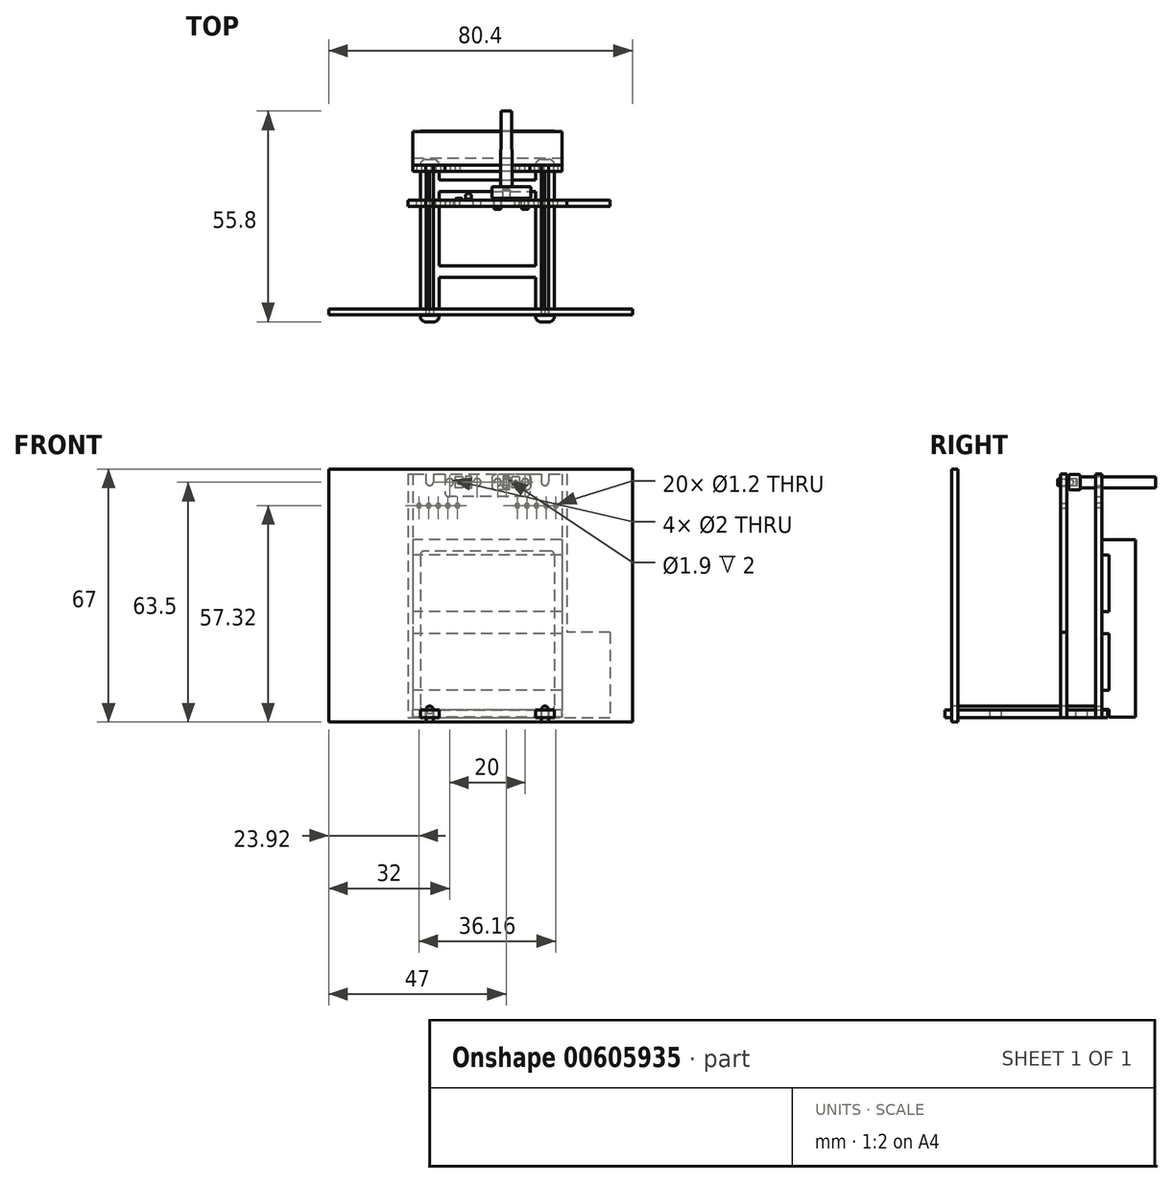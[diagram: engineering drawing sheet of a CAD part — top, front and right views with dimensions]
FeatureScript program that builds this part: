
annotation { "Feature Type Name" : "Feature", "Feature Type Description" : "" }
export const myFeature = defineFeature(function(context is Context, id is Id, definition is map)
    precondition{}
    {
        {
            var Q0;
            Q0=qCreatedBy(makeId("Top.planeOp"),FACE);
            var sketch = newSketch(context, id + "F0", { "sketchPlane" : qUnion([Q0])});
            skLineSegment(sketch, "E0", {"start": v(-17.75, -15.65) * mm, "end": v(-17.75, -13.85) * mm});
            skLineSegment(sketch, "E1", {"start": v(-17.75, -13.85) * mm, "end": v(-16.2, -13.85) * mm});
            skLineSegment(sketch, "E2", {"start": v(-16.2, -13.85) * mm, "end": v(-16.2, -12.2) * mm});
            skLineSegment(sketch, "E3", {"start": v(-16.2, -12.2) * mm, "end": v(-17.75, -12.2) * mm});
            skLineSegment(sketch, "E4", {"start": v(-14.3, -12.2) * mm, "end": v(-14.3, -13.85) * mm});
            skLineSegment(sketch, "E5", {"start": v(-14.3, -13.85) * mm, "end": v(-12.75, -13.85) * mm});
            skLineSegment(sketch, "E6", {"start": v(-12.75, -13.85) * mm, "end": v(-12.75, -15.65) * mm});
            skLineSegment(sketch, "E7", {"start": v(-12.75, -15.65) * mm, "end": v(-17.75, -15.65) * mm});
            skLineSegment(sketch, "E8", {"start": v(-12.75, -12.2) * mm, "end": v(-12.75, -3.84) * mm});
            skLineSegment(sketch, "E9", {"start": v(-12.75, -3.84) * mm, "end": v(12.75, -3.84) * mm});
            skLineSegment(sketch, "E10", {"start": v(17.75, 14.95) * mm, "end": v(16.2, 14.95) * mm});
            skLineSegment(sketch, "E11", {"start": v(16.2, 14.95) * mm, "end": v(16.2, 16.6) * mm});
            skLineSegment(sketch, "E12", {"start": v(16.2, 16.6) * mm, "end": v(17.75, 16.6) * mm});
            skLineSegment(sketch, "E13", {"start": v(17.75, 16.6) * mm, "end": v(17.75, 24.2) * mm});
            skLineSegment(sketch, "E14", {"start": v(12.75, 16.6) * mm, "end": v(14.3, 16.6) * mm});
            skLineSegment(sketch, "E15", {"start": v(14.3, 16.6) * mm, "end": v(14.3, 14.95) * mm});
            skLineSegment(sketch, "E16", {"start": v(14.3, 14.95) * mm, "end": v(12.75, 14.95) * mm});
            skLineSegment(sketch, "E17", {"start": v(-12.75, -0.84) * mm, "end": v(12.75, -0.84) * mm});
            skLineSegment(sketch, "E18", {"start": v(-17.75, 24.2) * mm, "end": v(-16.2, 24.2) * mm});
            skLineSegment(sketch, "E19", {"start": v(-16.2, 24.2) * mm, "end": v(-16.2, 25.85) * mm});
            skLineSegment(sketch, "E20", {"start": v(-16.2, 25.85) * mm, "end": v(-17.75, 25.85) * mm});
            skLineSegment(sketch, "E21", {"start": v(-17.75, 25.85) * mm, "end": v(-17.75, 27.35) * mm});
            skLineSegment(sketch, "E22", {"start": v(-17.75, 27.35) * mm, "end": v(-12.75, 27.35) * mm});
            skLineSegment(sketch, "E23", {"start": v(-12.75, 24.2) * mm, "end": v(-14.3, 24.2) * mm});
            skLineSegment(sketch, "E24", {"start": v(-14.3, 24.2) * mm, "end": v(-14.3, 25.85) * mm});
            skLineSegment(sketch, "E25", {"start": v(-14.3, 25.85) * mm, "end": v(-12.75, 25.85) * mm});
            skLineSegment(sketch, "E26", {"start": v(-12.75, 25.85) * mm, "end": v(-12.75, 27.35) * mm});
            skLineSegment(sketch, "E27", {"start": v(12.75, 24.2) * mm, "end": v(14.3, 24.2) * mm});
            skLineSegment(sketch, "E28", {"start": v(14.3, 25.85) * mm, "end": v(12.75, 25.85) * mm});
            skLineSegment(sketch, "E29", {"start": v(12.75, 25.85) * mm, "end": v(12.75, 27.35) * mm});
            skLineSegment(sketch, "E30", {"start": v(12.75, 27.35) * mm, "end": v(17.75, 27.35) * mm});
            skLineSegment(sketch, "E31", {"start": v(17.75, 24.2) * mm, "end": v(16.2, 24.2) * mm});
            skLineSegment(sketch, "E32", {"start": v(16.2, 24.2) * mm, "end": v(16.2, 25.85) * mm});
            skLineSegment(sketch, "E33", {"start": v(16.2, 25.85) * mm, "end": v(17.75, 25.85) * mm});
            skLineSegment(sketch, "E34", {"start": v(17.75, 25.85) * mm, "end": v(17.75, 27.35) * mm});
            skLineSegment(sketch, "E35", {"start": v(-12.75, -12.2) * mm, "end": v(-14.3, -12.2) * mm});
            skLineSegment(sketch, "E36", {"start": v(-12.75, 16.6) * mm, "end": v(-14.3, 16.6) * mm});
            skLineSegment(sketch, "E37", {"start": v(-14.3, 16.6) * mm, "end": v(-14.3, 14.95) * mm});
            skLineSegment(sketch, "E38", {"start": v(-14.3, 14.95) * mm, "end": v(-12.75, 14.95) * mm});
            skLineSegment(sketch, "E39", {"start": v(-12.75, -0.84) * mm, "end": v(-12.75, 14.95) * mm});
            skLineSegment(sketch, "E40", {"start": v(-17.75, 24.2) * mm, "end": v(-17.75, 16.6) * mm});
            skLineSegment(sketch, "E41", {"start": v(-17.75, 16.6) * mm, "end": v(-16.2, 16.6) * mm});
            skLineSegment(sketch, "E42", {"start": v(-16.2, 16.6) * mm, "end": v(-16.2, 14.95) * mm});
            skLineSegment(sketch, "E43", {"start": v(-16.2, 14.95) * mm, "end": v(-17.75, 14.95) * mm});
            skLineSegment(sketch, "E44", {"start": v(-17.75, 14.95) * mm, "end": v(-17.75, -12.2) * mm});
            skLineSegment(sketch, "E45", {"start": v(-12.75, 24.2) * mm, "end": v(-12.75, 21.9) * mm});
            skLineSegment(sketch, "E46", {"start": v(-12.75, 16.6) * mm, "end": v(-12.75, 18.82) * mm});
            skLineSegment(sketch, "E47", {"start": v(14.3, 25.85) * mm, "end": v(14.3, 24.2) * mm});
            skLineSegment(sketch, "E48", {"start": v(12.75, 24.2) * mm, "end": v(12.75, 21.9) * mm});
            skLineSegment(sketch, "E49", {"start": v(-12.75, 21.9) * mm, "end": v(12.75, 21.9) * mm});
            skLineSegment(sketch, "E50", {"start": v(-12.75, 18.82) * mm, "end": v(12.75, 18.82) * mm});
            skLineSegment(sketch, "E51", {"start": v(12.75, 16.6) * mm, "end": v(12.75, 18.82) * mm});
            skLineSegment(sketch, "E52", {"start": v(12.75, -0.84) * mm, "end": v(12.75, 14.95) * mm});
            skLineSegment(sketch, "E53", {"start": v(17.75, 14.95) * mm, "end": v(17.75, -12.2) * mm});
            skLineSegment(sketch, "E54", {"start": v(17.75, -12.2) * mm, "end": v(16.2, -12.2) * mm});
            skLineSegment(sketch, "E55", {"start": v(16.2, -12.2) * mm, "end": v(16.2, -13.85) * mm});
            skLineSegment(sketch, "E56", {"start": v(16.2, -13.85) * mm, "end": v(17.75, -13.85) * mm});
            skLineSegment(sketch, "E57", {"start": v(17.75, -13.85) * mm, "end": v(17.75, -15.65) * mm});
            skLineSegment(sketch, "E58", {"start": v(17.75, -15.65) * mm, "end": v(12.75, -15.65) * mm});
            skLineSegment(sketch, "E59", {"start": v(12.75, -15.65) * mm, "end": v(12.75, -13.85) * mm});
            skLineSegment(sketch, "E60", {"start": v(12.75, -13.85) * mm, "end": v(14.3, -13.85) * mm});
            skLineSegment(sketch, "E61", {"start": v(14.3, -13.85) * mm, "end": v(14.3, -12.2) * mm});
            skLineSegment(sketch, "E62", {"start": v(14.3, -12.2) * mm, "end": v(12.75, -12.2) * mm});
            skLineSegment(sketch, "E63", {"start": v(12.75, -12.2) * mm, "end": v(12.75, -3.84) * mm});
            skSolve(sketch);
        }
        {
            var Q0;
            Q0 = qSketchRegion(id + "F0", true);
            extrude(context, id + "F1", {"entities" : qUnion([Q0]), "depth" : 2 * mm, "offsetDistance" : 25 * mm});
        }
        {
            var Q0;
            Q0=makeQuery(id+"F1.opExtrude","SWEPT_EDGE",EDGE,{"disambiguationData":[OSD([sQuery(id+"F0.wireOp",EDGE,"E30"),sQuery(id+"F0.wireOp",EDGE,"E34")])]});
            var Q1;
            Q1=makeQuery(id+"F1.opExtrude","SWEPT_EDGE",EDGE,{"disambiguationData":[OSD([sQuery(id+"F0.wireOp",EDGE,"E29"),sQuery(id+"F0.wireOp",EDGE,"E30")])]});
            var Q2;
            Q2=makeQuery(id+"F1.opExtrude","SWEPT_EDGE",EDGE,{"disambiguationData":[OSD([sQuery(id+"F0.wireOp",EDGE,"E22"),sQuery(id+"F0.wireOp",EDGE,"E26")])]});
            var Q3;
            Q3=makeQuery(id+"F1.opExtrude","SWEPT_EDGE",EDGE,{"disambiguationData":[OSD([sQuery(id+"F0.wireOp",EDGE,"E21"),sQuery(id+"F0.wireOp",EDGE,"E22")])]});
            var Q4;
            Q4=makeQuery(id+"F1.opExtrude","SWEPT_EDGE",EDGE,{"disambiguationData":[OSD([sQuery(id+"F0.wireOp",EDGE,"6rP2uiYR-0tbi-BP4j-9BnD-fJcQIXdOzZpO"),sQuery(id+"F0.wireOp",EDGE,"r8ZNU0i4-ts59-kxLk-rAzM-9zbr7o6BRmU6")])]});
            var Q5;
            Q5=makeQuery(id+"F1.opExtrude","SWEPT_EDGE",EDGE,{"disambiguationData":[OSD([sQuery(id+"F0.wireOp",EDGE,"PC1FmKQ7-zntm-aZSk-GLTm-THbfAtVsDeOE"),sQuery(id+"F0.wireOp",EDGE,"6rP2uiYR-0tbi-BP4j-9BnD-fJcQIXdOzZpO")])]});
            var Q6;
            Q6=makeQuery(id+"F1.opExtrude","SWEPT_EDGE",EDGE,{"disambiguationData":[OSD([sQuery(id+"F0.wireOp",EDGE,"E6"),sQuery(id+"F0.wireOp",EDGE,"E7")])]});
            var Q7;
            Q7=makeQuery(id+"F1.opExtrude","SWEPT_EDGE",EDGE,{"disambiguationData":[OSD([sQuery(id+"F0.wireOp",EDGE,"E0"),sQuery(id+"F0.wireOp",EDGE,"E7")])]});
            var Q8;
            Q8=makeQuery(id+"F1.opExtrude","SWEPT_EDGE",EDGE,{"disambiguationData":[OSD([sQuery(id+"F0.wireOp",EDGE,"E57"),sQuery(id+"F0.wireOp",EDGE,"E58")])]});
            var Q9;
            Q9=makeQuery(id+"F1.opExtrude","SWEPT_EDGE",EDGE,{"disambiguationData":[OSD([sQuery(id+"F0.wireOp",EDGE,"E58"),sQuery(id+"F0.wireOp",EDGE,"E59")])]});
            fillet(context, id + "F2", {"entities" : qUnion([Q0, Q1, Q2, Q3, Q4, Q5, Q6, Q7, Q8, Q9]), "radius" : 1.5 * mm, "tangentPropagation" : true, "allowEdgeOverflow" : false});
        }
        {
            var Q0;
            Q0=makeQuery(id+"F1.opExtrude","CAP_FACE",FACE,{"disambiguationData":[OSD([sQuery(id+"F0.wireOp",EDGE,"E0"),sQuery(id+"F0.wireOp",EDGE,"E1"),sQuery(id+"F0.wireOp",EDGE,"E2"),sQuery(id+"F0.wireOp",EDGE,"E3"),sQuery(id+"F0.wireOp",EDGE,"E4"),sQuery(id+"F0.wireOp",EDGE,"E5"),sQuery(id+"F0.wireOp",EDGE,"E6"),sQuery(id+"F0.wireOp",EDGE,"E7"),sQuery(id+"F0.wireOp",EDGE,"E8"),sQuery(id+"F0.wireOp",EDGE,"E9"),sQuery(id+"F0.wireOp",EDGE,"E10"),sQuery(id+"F0.wireOp",EDGE,"E11"),sQuery(id+"F0.wireOp",EDGE,"E12"),sQuery(id+"F0.wireOp",EDGE,"E13"),sQuery(id+"F0.wireOp",EDGE,"E14"),sQuery(id+"F0.wireOp",EDGE,"E15"),sQuery(id+"F0.wireOp",EDGE,"E16"),sQuery(id+"F0.wireOp",EDGE,"E17"),sQuery(id+"F0.wireOp",EDGE,"E18"),sQuery(id+"F0.wireOp",EDGE,"E19"),sQuery(id+"F0.wireOp",EDGE,"E20"),sQuery(id+"F0.wireOp",EDGE,"E21"),sQuery(id+"F0.wireOp",EDGE,"E22"),sQuery(id+"F0.wireOp",EDGE,"E23"),sQuery(id+"F0.wireOp",EDGE,"E24"),sQuery(id+"F0.wireOp",EDGE,"E25"),sQuery(id+"F0.wireOp",EDGE,"E26"),sQuery(id+"F0.wireOp",EDGE,"E27"),sQuery(id+"F0.wireOp",EDGE,"E28"),sQuery(id+"F0.wireOp",EDGE,"E29"),sQuery(id+"F0.wireOp",EDGE,"E30"),sQuery(id+"F0.wireOp",EDGE,"E31"),sQuery(id+"F0.wireOp",EDGE,"E32"),sQuery(id+"F0.wireOp",EDGE,"E33"),sQuery(id+"F0.wireOp",EDGE,"E34"),sQuery(id+"F0.wireOp",EDGE,"E35"),sQuery(id+"F0.wireOp",EDGE,"E36"),sQuery(id+"F0.wireOp",EDGE,"E37"),sQuery(id+"F0.wireOp",EDGE,"E38"),sQuery(id+"F0.wireOp",EDGE,"E39"),sQuery(id+"F0.wireOp",EDGE,"E40"),sQuery(id+"F0.wireOp",EDGE,"E41"),sQuery(id+"F0.wireOp",EDGE,"E42"),sQuery(id+"F0.wireOp",EDGE,"E43"),sQuery(id+"F0.wireOp",EDGE,"E44"),sQuery(id+"F0.wireOp",EDGE,"E45"),sQuery(id+"F0.wireOp",EDGE,"E46"),sQuery(id+"F0.wireOp",EDGE,"E47"),sQuery(id+"F0.wireOp",EDGE,"E48"),sQuery(id+"F0.wireOp",EDGE,"E49"),sQuery(id+"F0.wireOp",EDGE,"E50"),sQuery(id+"F0.wireOp",EDGE,"E51"),sQuery(id+"F0.wireOp",EDGE,"E52"),sQuery(id+"F0.wireOp",EDGE,"E53"),sQuery(id+"F0.wireOp",EDGE,"E54"),sQuery(id+"F0.wireOp",EDGE,"E55"),sQuery(id+"F0.wireOp",EDGE,"E56"),sQuery(id+"F0.wireOp",EDGE,"E57"),sQuery(id+"F0.wireOp",EDGE,"E58"),sQuery(id+"F0.wireOp",EDGE,"E59"),sQuery(id+"F0.wireOp",EDGE,"E60"),sQuery(id+"F0.wireOp",EDGE,"E61"),sQuery(id+"F0.wireOp",EDGE,"E62"),sQuery(id+"F0.wireOp",EDGE,"E63")])],"isStart":false});
            var sketch = newSketch(context, id + "F3", { "sketchPlane" : qUnion([Q0])});
            skLineSegment(sketch, "E64.bottom", {"start": v(-16.2, 25.85) * mm, "end": v(-14.3, 25.85) * mm});
            skLineSegment(sketch, "E64.top", {"start": v(-16.2, -13.85) * mm, "end": v(-14.3, -13.85) * mm});
            skLineSegment(sketch, "E64.left", {"start": v(-16.2, 25.85) * mm, "end": v(-16.2, -13.85) * mm});
            skLineSegment(sketch, "E64.right", {"start": v(-14.3, 25.85) * mm, "end": v(-14.3, -13.85) * mm});
            skLineSegment(sketch, "E65.bottom", {"start": v(14.3, 25.85) * mm, "end": v(16.2, 25.85) * mm});
            skLineSegment(sketch, "E65.top", {"start": v(14.3, -13.85) * mm, "end": v(16.2, -13.85) * mm});
            skLineSegment(sketch, "E65.left", {"start": v(14.3, 25.85) * mm, "end": v(14.3, -13.85) * mm});
            skLineSegment(sketch, "E65.right", {"start": v(16.2, 25.85) * mm, "end": v(16.2, -13.85) * mm});
            skSolve(sketch);
        }
        {
            var Q0;
            Q0 = qSketchRegion(id + "F3", true);
            extrude(context, id + "F4", {"entities" : qUnion([Q0]), "operationType" : NewBodyOperationType.ADD, "depth" : 1 * mm, "offsetDistance" : 25 * mm});
        }
        {
            var Q0;
            Q0=makeQuery(id+"F4.opExtrude","CAP_EDGE",EDGE,{"disambiguationData":[OSD([sQuery(id+"F3.wireOp",EDGE,"E64.right")])],"isStart":false});
            var Q1;
            Q1=makeQuery(id+"F4.opExtrude","CAP_EDGE",EDGE,{"disambiguationData":[OSD([sQuery(id+"F3.wireOp",EDGE,"E64.left")])],"isStart":false});
            var Q2;
            Q2=makeQuery(id+"F4.opExtrude","CAP_EDGE",EDGE,{"disambiguationData":[OSD([sQuery(id+"F3.wireOp",EDGE,"E65.right")])],"isStart":false});
            var Q3;
            Q3=makeQuery(id+"F4.opExtrude","CAP_EDGE",EDGE,{"disambiguationData":[OSD([sQuery(id+"F3.wireOp",EDGE,"E65.left")])],"isStart":false});
            fillet(context, id + "F5", {"entities" : qUnion([Q0, Q1, Q2, Q3]), "radius" : 1 * mm, "tangentPropagation" : true, "allowEdgeOverflow" : false});
        }
        {
            var Q0;
            Q0=makeQuery(id+"F1.opExtrude","CAP_FACE",FACE,{"disambiguationData":[OSD([sQuery(id+"F0.wireOp",EDGE,"E0"),sQuery(id+"F0.wireOp",EDGE,"E1"),sQuery(id+"F0.wireOp",EDGE,"E2"),sQuery(id+"F0.wireOp",EDGE,"E3"),sQuery(id+"F0.wireOp",EDGE,"E4"),sQuery(id+"F0.wireOp",EDGE,"E5"),sQuery(id+"F0.wireOp",EDGE,"E6"),sQuery(id+"F0.wireOp",EDGE,"E7"),sQuery(id+"F0.wireOp",EDGE,"E8"),sQuery(id+"F0.wireOp",EDGE,"E9"),sQuery(id+"F0.wireOp",EDGE,"E10"),sQuery(id+"F0.wireOp",EDGE,"E11"),sQuery(id+"F0.wireOp",EDGE,"E12"),sQuery(id+"F0.wireOp",EDGE,"E13"),sQuery(id+"F0.wireOp",EDGE,"E14"),sQuery(id+"F0.wireOp",EDGE,"E15"),sQuery(id+"F0.wireOp",EDGE,"E16"),sQuery(id+"F0.wireOp",EDGE,"E17"),sQuery(id+"F0.wireOp",EDGE,"E18"),sQuery(id+"F0.wireOp",EDGE,"E19"),sQuery(id+"F0.wireOp",EDGE,"E20"),sQuery(id+"F0.wireOp",EDGE,"E21"),sQuery(id+"F0.wireOp",EDGE,"E22"),sQuery(id+"F0.wireOp",EDGE,"E23"),sQuery(id+"F0.wireOp",EDGE,"E24"),sQuery(id+"F0.wireOp",EDGE,"E25"),sQuery(id+"F0.wireOp",EDGE,"E26"),sQuery(id+"F0.wireOp",EDGE,"E27"),sQuery(id+"F0.wireOp",EDGE,"E28"),sQuery(id+"F0.wireOp",EDGE,"E29"),sQuery(id+"F0.wireOp",EDGE,"E30"),sQuery(id+"F0.wireOp",EDGE,"E31"),sQuery(id+"F0.wireOp",EDGE,"E32"),sQuery(id+"F0.wireOp",EDGE,"E33"),sQuery(id+"F0.wireOp",EDGE,"E34"),sQuery(id+"F0.wireOp",EDGE,"E35"),sQuery(id+"F0.wireOp",EDGE,"E36"),sQuery(id+"F0.wireOp",EDGE,"E37"),sQuery(id+"F0.wireOp",EDGE,"E38"),sQuery(id+"F0.wireOp",EDGE,"E39"),sQuery(id+"F0.wireOp",EDGE,"E40"),sQuery(id+"F0.wireOp",EDGE,"E41"),sQuery(id+"F0.wireOp",EDGE,"E42"),sQuery(id+"F0.wireOp",EDGE,"E43"),sQuery(id+"F0.wireOp",EDGE,"E44"),sQuery(id+"F0.wireOp",EDGE,"E45"),sQuery(id+"F0.wireOp",EDGE,"E46"),sQuery(id+"F0.wireOp",EDGE,"E47"),sQuery(id+"F0.wireOp",EDGE,"E48"),sQuery(id+"F0.wireOp",EDGE,"E49"),sQuery(id+"F0.wireOp",EDGE,"E50"),sQuery(id+"F0.wireOp",EDGE,"E51"),sQuery(id+"F0.wireOp",EDGE,"E52"),sQuery(id+"F0.wireOp",EDGE,"E53"),sQuery(id+"F0.wireOp",EDGE,"E54"),sQuery(id+"F0.wireOp",EDGE,"E55"),sQuery(id+"F0.wireOp",EDGE,"E56"),sQuery(id+"F0.wireOp",EDGE,"E57"),sQuery(id+"F0.wireOp",EDGE,"E58"),sQuery(id+"F0.wireOp",EDGE,"E59"),sQuery(id+"F0.wireOp",EDGE,"E60"),sQuery(id+"F0.wireOp",EDGE,"E61"),sQuery(id+"F0.wireOp",EDGE,"E62"),sQuery(id+"F0.wireOp",EDGE,"E63")])],"isStart":true});
            var sketch = newSketch(context, id + "F6", { "sketchPlane" : qUnion([Q0])});
            skLineSegment(sketch, "E66.bottom", {"start": v(-16.2, 13.85) * mm, "end": v(-14.3, 13.85) * mm});
            skLineSegment(sketch, "E66.top", {"start": v(-16.2, 12.2) * mm, "end": v(-14.3, 12.2) * mm});
            skLineSegment(sketch, "E66.left", {"start": v(-16.2, 13.85) * mm, "end": v(-16.2, 12.2) * mm});
            skLineSegment(sketch, "E66.right", {"start": v(-14.3, 13.85) * mm, "end": v(-14.3, 12.2) * mm});
            skLineSegment(sketch, "E67.bottom", {"start": v(14.3, 13.85) * mm, "end": v(16.2, 13.85) * mm});
            skLineSegment(sketch, "E67.top", {"start": v(14.3, 12.2) * mm, "end": v(16.2, 12.2) * mm});
            skLineSegment(sketch, "E67.left", {"start": v(14.3, 13.85) * mm, "end": v(14.3, 12.2) * mm});
            skLineSegment(sketch, "E67.right", {"start": v(16.2, 13.85) * mm, "end": v(16.2, 12.2) * mm});
            skSolve(sketch);
        }
        {
            var Q0;
            Q0 = qSketchRegion(id + "F6", true);
            extrude(context, id + "F7", {"entities" : qUnion([Q0]), "operationType" : NewBodyOperationType.ADD, "depth" : 1.25 * mm, "offsetDistance" : 25 * mm});
        }
        {
            var Q0;
            Q0=makeQuery(id+"F7.opExtrude","CAP_EDGE",EDGE,{"disambiguationData":[OSD([sQuery(id+"F6.wireOp",EDGE,"E66.right")])],"isStart":false});
            var Q1;
            Q1=makeQuery(id+"F7.opExtrude","CAP_EDGE",EDGE,{"disambiguationData":[OSD([sQuery(id+"F6.wireOp",EDGE,"E66.left")])],"isStart":false});
            var Q2;
            Q2=makeQuery(id+"F7.opExtrude","CAP_EDGE",EDGE,{"disambiguationData":[OSD([sQuery(id+"F6.wireOp",EDGE,"E67.right")])],"isStart":false});
            var Q3;
            Q3=makeQuery(id+"F7.opExtrude","CAP_EDGE",EDGE,{"disambiguationData":[OSD([sQuery(id+"F6.wireOp",EDGE,"E67.left")])],"isStart":false});
            fillet(context, id + "F8", {"entities" : qUnion([Q0, Q1, Q2, Q3]), "radius" : 0.3 * mm, "tangentPropagation" : true, "allowEdgeOverflow" : false});
        }
        {
            var Q0;
            {var subQ0=sQuery(id+"F0.wireOp",EDGE,"E54");var subQ1=sQuery(id+"F0.wireOp",EDGE,"E53");var subQ2=sQuery(id+"F0.wireOp",EDGE,"E52");var subQ3=sQuery(id+"F0.wireOp",EDGE,"E48");var subQ4=sQuery(id+"F0.wireOp",EDGE,"E47");var subQ5=sQuery(id+"F0.wireOp",EDGE,"E46");var subQ6=sQuery(id+"F0.wireOp",EDGE,"E45");var subQ7=sQuery(id+"F0.wireOp",EDGE,"E44");var subQ8=sQuery(id+"F0.wireOp",EDGE,"E43");var subQ9=sQuery(id+"F0.wireOp",EDGE,"E42");var subQ10=sQuery(id+"F0.wireOp",EDGE,"E41");var subQ11=sQuery(id+"F0.wireOp",EDGE,"E40");var subQ12=sQuery(id+"F0.wireOp",EDGE,"E39");var subQ13=sQuery(id+"F0.wireOp",EDGE,"E38");var subQ14=sQuery(id+"F0.wireOp",EDGE,"E37");var subQ15=sQuery(id+"F0.wireOp",EDGE,"E36");var subQ16=sQuery(id+"F0.wireOp",EDGE,"E35");var subQ17=sQuery(id+"F0.wireOp",EDGE,"E33");var subQ18=sQuery(id+"F0.wireOp",EDGE,"E32");var subQ19=sQuery(id+"F0.wireOp",EDGE,"E31");var subQ20=sQuery(id+"F0.wireOp",EDGE,"E30");var subQ21=sQuery(id+"F0.wireOp",EDGE,"E12");var subQ22=sQuery(id+"F0.wireOp",EDGE,"E11");var subQ23=sQuery(id+"F0.wireOp",EDGE,"E10");var subQ24=sQuery(id+"F0.wireOp",EDGE,"E9");var subQ25=sQuery(id+"F0.wireOp",EDGE,"E34");var subQ26=sQuery(id+"F0.wireOp",EDGE,"E13");var subQ27=sQuery(id+"F0.wireOp",EDGE,"E49");var subQ28=sQuery(id+"F0.wireOp",EDGE,"E2");var subQ29=sQuery(id+"F0.wireOp",EDGE,"E25");var subQ30=sQuery(id+"F0.wireOp",EDGE,"E14");var subQ31=sQuery(id+"F0.wireOp",EDGE,"E50");var subQ32=sQuery(id+"F0.wireOp",EDGE,"E3");var subQ33=sQuery(id+"F0.wireOp",EDGE,"E8");var subQ34=sQuery(id+"F0.wireOp",EDGE,"E29");var subQ35=sQuery(id+"F0.wireOp",EDGE,"E51");var subQ36=sQuery(id+"F0.wireOp",EDGE,"E4");var subQ37=sQuery(id+"F0.wireOp",EDGE,"E27");var subQ38=sQuery(id+"F0.wireOp",EDGE,"E15");var subQ39=sQuery(id+"F0.wireOp",EDGE,"E16");var subQ40=sQuery(id+"F0.wireOp",EDGE,"E17");var subQ41=sQuery(id+"F0.wireOp",EDGE,"E18");var subQ42=sQuery(id+"F0.wireOp",EDGE,"E19");var subQ43=sQuery(id+"F0.wireOp",EDGE,"E20");var subQ44=sQuery(id+"F0.wireOp",EDGE,"E22");var subQ45=sQuery(id+"F0.wireOp",EDGE,"E23");var subQ46=sQuery(id+"F0.wireOp",EDGE,"E24");var subQ47=sQuery(id+"F0.wireOp",EDGE,"E28");var subQ48=sQuery(id+"F0.wireOp",EDGE,"E55");var subQ49=sQuery(id+"F0.wireOp",EDGE,"E61");var subQ50=sQuery(id+"F0.wireOp",EDGE,"E62");var subQ51=sQuery(id+"F0.wireOp",EDGE,"E63");var subQ52=sQuery(id+"F0.wireOp",EDGE,"E21");var subQ53=sQuery(id+"F0.wireOp",EDGE,"E26");Q0=makeQuery(id+"F7.boolean.opBoolean","SPLIT",FACE,{"disambiguationData":[TD([makeQuery(id+"F1.opExtrude","SWEPT_FACE",FACE,{"disambiguationData":[OSD([subQ32])]})])],"derivedFrom":makeQuery(id+"F1.opExtrude","CAP_FACE",FACE,{"disambiguationData":[OSD([sQuery(id+"F0.wireOp",EDGE,"E0"),sQuery(id+"F0.wireOp",EDGE,"E1"),subQ28,subQ32,subQ36,sQuery(id+"F0.wireOp",EDGE,"E5"),sQuery(id+"F0.wireOp",EDGE,"E6"),sQuery(id+"F0.wireOp",EDGE,"E7"),subQ33,subQ24,subQ23,subQ22,subQ21,subQ26,subQ30,subQ38,subQ39,subQ40,subQ41,subQ42,subQ43,subQ52,subQ44,subQ45,subQ46,subQ29,subQ53,subQ37,subQ47,subQ34,subQ20,subQ19,subQ18,subQ17,subQ25,subQ16,subQ15,subQ14,subQ13,subQ12,subQ11,subQ10,subQ9,subQ8,subQ7,subQ6,subQ5,subQ4,subQ3,subQ27,subQ31,subQ35,subQ2,subQ1,subQ0,subQ48,sQuery(id+"F0.wireOp",EDGE,"E56"),sQuery(id+"F0.wireOp",EDGE,"E57"),sQuery(id+"F0.wireOp",EDGE,"E58"),sQuery(id+"F0.wireOp",EDGE,"E59"),sQuery(id+"F0.wireOp",EDGE,"E60"),subQ49,subQ50,subQ51])],"isStart":true})});}
            var sketch = newSketch(context, id + "F9", { "sketchPlane" : qUnion([Q0])});
            skLineSegment(sketch, "E68.bottom", {"start": v(-19.75, -24.22) * mm, "end": v(19.75, -24.22) * mm});
            skLineSegment(sketch, "E68.top", {"start": v(-19.75, -25.82) * mm, "end": v(19.75, -25.82) * mm});
            skLineSegment(sketch, "E68.left", {"start": v(-19.75, -24.22) * mm, "end": v(-19.75, -25.82) * mm});
            skLineSegment(sketch, "E68.right", {"start": v(19.75, -24.22) * mm, "end": v(19.75, -25.82) * mm});
            skSolve(sketch);
        }
        {
            var Q0;
            Q0 = qSketchRegion(id + "F9", true);
            extrude(context, id + "F10", {"entities" : qUnion([Q0]), "oppositeDirection" : true, "depth" : 64.5 * mm, "offsetDistance" : 25 * mm});
        }
        {
            var Q0;
            Q0=makeQuery(id+"F10.opExtrude","SWEPT_FACE",FACE,{"disambiguationData":[OSD([sQuery(id+"F9.wireOp",EDGE,"E68.top")])]});
            var sketch = newSketch(context, id + "F11", { "sketchPlane" : qUnion([Q0])});
            skLineSegment(sketch, "E69.bottom", {"start": v(-16.25, 0) * mm, "end": v(-14.25, 0) * mm});
            skLineSegment(sketch, "E69.left", {"start": v(-16.25, 0) * mm, "end": v(-16.25, 2) * mm});
            skLineSegment(sketch, "E69.right", {"start": v(-14.25, 0) * mm, "end": v(-14.25, 2) * mm});
            skArc(sketch, "E70", {"start": v(-14.25, 2) * mm, "mid": v(-15.25, 3.04) * mm, "end": v(-16.25, 2) * mm});
            skLineSegment(sketch, "E71.bottom", {"start": v(14.25, 0) * mm, "end": v(16.25, 0) * mm});
            skLineSegment(sketch, "E71.left", {"start": v(14.25, 0) * mm, "end": v(14.25, 2) * mm});
            skLineSegment(sketch, "E71.right", {"start": v(16.25, 0) * mm, "end": v(16.25, 2) * mm});
            skArc(sketch, "E72", {"start": v(16.25, 2) * mm, "mid": v(15.25, 3.04) * mm, "end": v(14.25, 2) * mm});
            skSolve(sketch);
        }
        {
            var Q0;
            Q0 = qSketchRegion(id + "F11", true);
            extrude(context, id + "F12", {"entities" : qUnion([Q0]), "operationType" : NewBodyOperationType.REMOVE, "oppositeDirection" : true, "depth" : 1.65 * mm, "offsetDistance" : 25 * mm});
        }
        {
            var Q0;
            Q0=makeQuery(id+"F10.opExtrude","SWEPT_FACE",FACE,{"disambiguationData":[OSD([sQuery(id+"F9.wireOp",EDGE,"E68.top")])]});
            var sketch = newSketch(context, id + "F13", { "sketchPlane" : qUnion([Q0])});
            skLineSegment(sketch, "E73.bottom", {"start": v(-11.25, 64.5) * mm, "end": v(11.25, 64.5) * mm});
            skLineSegment(sketch, "E73.top", {"start": v(-11.25, 58.5) * mm, "end": v(11.25, 58.5) * mm});
            skLineSegment(sketch, "E73.left", {"start": v(-11.25, 64.5) * mm, "end": v(-11.25, 58.5) * mm});
            skLineSegment(sketch, "E73.right", {"start": v(11.25, 64.5) * mm, "end": v(11.25, 58.5) * mm});
            skSolve(sketch);
        }
        {
            var Q0;
            Q0 = qSketchRegion(id + "F13", true);
            extrude(context, id + "F14", {"entities" : qUnion([Q0]), "operationType" : NewBodyOperationType.REMOVE, "oppositeDirection" : true, "depth" : 1.65 * mm, "offsetDistance" : 25 * mm});
        }
        {
            var Q0;
            Q0=makeQuery(id+"F10.opExtrude","SWEPT_FACE",FACE,{"disambiguationData":[OSD([sQuery(id+"F9.wireOp",EDGE,"E68.top")])]});
            var sketch = newSketch(context, id + "F15", { "sketchPlane" : qUnion([Q0])});
            skLineSegment(sketch, "E74.bottom", {"start": v(-16.25, 64.5) * mm, "end": v(-14.25, 64.5) * mm});
            skLineSegment(sketch, "E74.left", {"start": v(-16.25, 64.5) * mm, "end": v(-16.25, 62.4) * mm});
            skLineSegment(sketch, "E74.right", {"start": v(-14.25, 64.5) * mm, "end": v(-14.25, 62.4) * mm});
            skArc(sketch, "E75", {"start": v(-16.25, 62.4) * mm, "mid": v(-15.25, 61.4) * mm, "end": v(-14.25, 62.4) * mm});
            skLineSegment(sketch, "E76.bottom", {"start": v(14.25, 64.5) * mm, "end": v(16.25, 64.5) * mm});
            skLineSegment(sketch, "E76.left", {"start": v(14.25, 64.5) * mm, "end": v(14.25, 62.4) * mm});
            skLineSegment(sketch, "E76.right", {"start": v(16.25, 64.5) * mm, "end": v(16.25, 62.4) * mm});
            skArc(sketch, "E77", {"start": v(14.25, 62.4) * mm, "mid": v(15.25, 61.4) * mm, "end": v(16.25, 62.4) * mm});
            skSolve(sketch);
        }
        {
            var Q0;
            Q0 = qSketchRegion(id + "F15", true);
            extrude(context, id + "F16", {"entities" : qUnion([Q0]), "operationType" : NewBodyOperationType.REMOVE, "oppositeDirection" : true, "depth" : 1.65 * mm, "offsetDistance" : 25 * mm});
        }
        {
            var Q0;
            Q0=makeQuery(id+"F10.opExtrude","SWEPT_FACE",FACE,{"disambiguationData":[OSD([sQuery(id+"F9.wireOp",EDGE,"E68.top")])]});
            var sketch = newSketch(context, id + "F17", { "sketchPlane" : qUnion([Q0])});
            skLineSegment(sketch, "E78.bottom", {"start": v(-19.75, 47.1) * mm, "end": v(19.75, 47.1) * mm});
            skLineSegment(sketch, "E78.top", {"start": v(-19.75, 2.1) * mm, "end": v(19.75, 2.1) * mm});
            skLineSegment(sketch, "E78.left", {"start": v(-19.75, 47.1) * mm, "end": v(-19.75, 2.1) * mm});
            skLineSegment(sketch, "E78.right", {"start": v(19.75, 47.1) * mm, "end": v(19.75, 2.1) * mm});
            skSolve(sketch);
        }
        {
            var Q0;
            Q0 = qSketchRegion(id + "F17", true);
            extrude(context, id + "F18", {"entities" : qUnion([Q0]), "depth" : 8.9 * mm, "offsetDistance" : 25 * mm});
        }
        {
            var Q0;
            Q0=makeQuery(id+"F18.opExtrude","SWEPT_FACE",FACE,{"disambiguationData":[OSD([sQuery(id+"F17.wireOp",EDGE,"E78.top")])]});
            var sketch = newSketch(context, id + "F19", { "sketchPlane" : qUnion([Q0])});
            skLineSegment(sketch, "E79.bottom", {"start": v(-19.75, -34.72) * mm, "end": v(19.75, -34.72) * mm});
            skLineSegment(sketch, "E79.top", {"start": v(-19.75, -27.82) * mm, "end": v(19.75, -27.82) * mm});
            skLineSegment(sketch, "E79.left", {"start": v(-19.75, -34.72) * mm, "end": v(-19.75, -27.82) * mm});
            skLineSegment(sketch, "E79.right", {"start": v(19.75, -34.72) * mm, "end": v(19.75, -27.82) * mm});
            skSolve(sketch);
        }
        {
            var Q0;
            Q0 = qSketchRegion(id + "F19", true);
            extrude(context, id + "F20", {"entities" : qUnion([Q0]), "operationType" : NewBodyOperationType.ADD, "depth" : 2 * mm, "offsetDistance" : 25 * mm});
        }
        {
            var Q0;
            Q0=makeQuery(id+"F20.boolean.opBoolean","MERGE",FACE,{"derivedFrom":[makeQuery(id+"F18.opExtrude","SWEPT_FACE",FACE,{"disambiguationData":[OSD([sQuery(id+"F17.wireOp",EDGE,"E78.right")])]}),makeQuery(id+"F20.opExtrude","SWEPT_FACE",FACE,{"disambiguationData":[OSD([sQuery(id+"F19.wireOp",EDGE,"E79.left")])]})]});
            var sketch = newSketch(context, id + "F21", { "sketchPlane" : qUnion([Q0])});
            skLineSegment(sketch, "E80.bottom", {"start": v(-25.82, 22.2) * mm, "end": v(-27.82, 22.2) * mm});
            skLineSegment(sketch, "E80.top", {"start": v(-25.82, 7.2) * mm, "end": v(-27.82, 7.2) * mm});
            skLineSegment(sketch, "E80.left", {"start": v(-25.82, 22.2) * mm, "end": v(-25.82, 7.2) * mm});
            skLineSegment(sketch, "E80.right", {"start": v(-27.82, 22.2) * mm, "end": v(-27.82, 7.2) * mm});
            skLineSegment(sketch, "E81.bottom", {"start": v(-25.82, 43) * mm, "end": v(-27.82, 43) * mm});
            skLineSegment(sketch, "E81.top", {"start": v(-25.82, 28) * mm, "end": v(-27.82, 28) * mm});
            skLineSegment(sketch, "E81.left", {"start": v(-25.82, 43) * mm, "end": v(-25.82, 28) * mm});
            skLineSegment(sketch, "E81.right", {"start": v(-27.82, 43) * mm, "end": v(-27.82, 28) * mm});
            skSolve(sketch);
        }
        {
            var Q0;
            Q0 = qSketchRegion(id + "F21", true);
            extrude(context, id + "F22", {"entities" : qUnion([Q0]), "operationType" : NewBodyOperationType.REMOVE, "oppositeDirection" : true, "depth" : 39.5 * mm, "offsetDistance" : 25 * mm});
        }
        {
            var Q0;
            Q0=makeQuery(id+"F20.boolean.opBoolean","MERGE",FACE,{"derivedFrom":[makeQuery(id+"F18.opExtrude","CAP_FACE",FACE,{"disambiguationData":[OSD([sQuery(id+"F17.wireOp",EDGE,"E78.bottom"),sQuery(id+"F17.wireOp",EDGE,"E78.top"),sQuery(id+"F17.wireOp",EDGE,"E78.left"),sQuery(id+"F17.wireOp",EDGE,"E78.right")])],"isStart":false}),makeQuery(id+"F20.opExtrude","SWEPT_FACE",FACE,{"disambiguationData":[OSD([sQuery(id+"F19.wireOp",EDGE,"E79.bottom")])]})]});
            var sketch = newSketch(context, id + "F23", { "sketchPlane" : qUnion([Q0])});
            skLineSegment(sketch, "E82.bottom", {"start": v(-17.75, 44) * mm, "end": v(17.75, 44) * mm});
            skLineSegment(sketch, "E82.top", {"start": v(-17.75, 2) * mm, "end": v(17.75, 2) * mm});
            skLineSegment(sketch, "E82.left", {"start": v(-17.75, 44) * mm, "end": v(-17.75, 2) * mm});
            skLineSegment(sketch, "E82.right", {"start": v(17.75, 44) * mm, "end": v(17.75, 2) * mm});
            skSolve(sketch);
        }
        {
            var Q0;
            Q0 = qSketchRegion(id + "F23", true);
            extrude(context, id + "F24", {"entities" : qUnion([Q0]), "depth" : 0.1 * mm, "offsetDistance" : 25 * mm});
        }
        {
            var Q0;
            Q0=makeQuery(id+"F24.opExtrude","SWEPT_EDGE",EDGE,{"disambiguationData":[OSD([sQuery(id+"F23.wireOp",EDGE,"E82.top"),sQuery(id+"F23.wireOp",EDGE,"E82.left")])]});
            var Q1;
            Q1=makeQuery(id+"F24.opExtrude","SWEPT_EDGE",EDGE,{"disambiguationData":[OSD([sQuery(id+"F23.wireOp",EDGE,"E82.bottom"),sQuery(id+"F23.wireOp",EDGE,"E82.left")])]});
            var Q2;
            Q2=makeQuery(id+"F24.opExtrude","SWEPT_EDGE",EDGE,{"disambiguationData":[OSD([sQuery(id+"F23.wireOp",EDGE,"E82.bottom"),sQuery(id+"F23.wireOp",EDGE,"E82.right")])]});
            var Q3;
            Q3=makeQuery(id+"F24.opExtrude","SWEPT_EDGE",EDGE,{"disambiguationData":[OSD([sQuery(id+"F23.wireOp",EDGE,"E82.top"),sQuery(id+"F23.wireOp",EDGE,"E82.right")])]});
            fillet(context, id + "F25", {"entities" : qUnion([Q0, Q1, Q2, Q3]), "radius" : 1 * mm, "tangentPropagation" : true, "allowEdgeOverflow" : false});
        }
        {
            var Q0;
            {var subQ0=sQuery(id+"F0.wireOp",EDGE,"E54");var subQ1=sQuery(id+"F0.wireOp",EDGE,"E53");var subQ2=sQuery(id+"F0.wireOp",EDGE,"E52");var subQ3=sQuery(id+"F0.wireOp",EDGE,"E48");var subQ4=sQuery(id+"F0.wireOp",EDGE,"E47");var subQ5=sQuery(id+"F0.wireOp",EDGE,"E46");var subQ6=sQuery(id+"F0.wireOp",EDGE,"E45");var subQ7=sQuery(id+"F0.wireOp",EDGE,"E44");var subQ8=sQuery(id+"F0.wireOp",EDGE,"E43");var subQ9=sQuery(id+"F0.wireOp",EDGE,"E42");var subQ10=sQuery(id+"F0.wireOp",EDGE,"E41");var subQ11=sQuery(id+"F0.wireOp",EDGE,"E40");var subQ12=sQuery(id+"F0.wireOp",EDGE,"E39");var subQ13=sQuery(id+"F0.wireOp",EDGE,"E38");var subQ14=sQuery(id+"F0.wireOp",EDGE,"E37");var subQ15=sQuery(id+"F0.wireOp",EDGE,"E36");var subQ16=sQuery(id+"F0.wireOp",EDGE,"E35");var subQ17=sQuery(id+"F0.wireOp",EDGE,"E33");var subQ18=sQuery(id+"F0.wireOp",EDGE,"E32");var subQ19=sQuery(id+"F0.wireOp",EDGE,"E31");var subQ20=sQuery(id+"F0.wireOp",EDGE,"E30");var subQ21=sQuery(id+"F0.wireOp",EDGE,"E12");var subQ22=sQuery(id+"F0.wireOp",EDGE,"E11");var subQ23=sQuery(id+"F0.wireOp",EDGE,"E10");var subQ24=sQuery(id+"F0.wireOp",EDGE,"E9");var subQ25=sQuery(id+"F0.wireOp",EDGE,"E34");var subQ26=sQuery(id+"F0.wireOp",EDGE,"E13");var subQ27=sQuery(id+"F0.wireOp",EDGE,"E49");var subQ28=sQuery(id+"F0.wireOp",EDGE,"E2");var subQ29=sQuery(id+"F0.wireOp",EDGE,"E25");var subQ30=sQuery(id+"F0.wireOp",EDGE,"E14");var subQ31=sQuery(id+"F0.wireOp",EDGE,"E50");var subQ32=sQuery(id+"F0.wireOp",EDGE,"E3");var subQ33=sQuery(id+"F0.wireOp",EDGE,"E8");var subQ34=sQuery(id+"F0.wireOp",EDGE,"E29");var subQ35=sQuery(id+"F0.wireOp",EDGE,"E51");var subQ36=sQuery(id+"F0.wireOp",EDGE,"E4");var subQ37=sQuery(id+"F0.wireOp",EDGE,"E27");var subQ38=sQuery(id+"F0.wireOp",EDGE,"E15");var subQ39=sQuery(id+"F0.wireOp",EDGE,"E16");var subQ40=sQuery(id+"F0.wireOp",EDGE,"E17");var subQ41=sQuery(id+"F0.wireOp",EDGE,"E18");var subQ42=sQuery(id+"F0.wireOp",EDGE,"E19");var subQ43=sQuery(id+"F0.wireOp",EDGE,"E20");var subQ44=sQuery(id+"F0.wireOp",EDGE,"E22");var subQ45=sQuery(id+"F0.wireOp",EDGE,"E23");var subQ46=sQuery(id+"F0.wireOp",EDGE,"E24");var subQ47=sQuery(id+"F0.wireOp",EDGE,"E28");var subQ48=sQuery(id+"F0.wireOp",EDGE,"E55");var subQ49=sQuery(id+"F0.wireOp",EDGE,"E61");var subQ50=sQuery(id+"F0.wireOp",EDGE,"E62");var subQ51=sQuery(id+"F0.wireOp",EDGE,"E63");var subQ52=sQuery(id+"F0.wireOp",EDGE,"E21");var subQ53=sQuery(id+"F0.wireOp",EDGE,"E26");Q0=makeQuery(id+"F7.boolean.opBoolean","SPLIT",FACE,{"disambiguationData":[TD([makeQuery(id+"F1.opExtrude","SWEPT_FACE",FACE,{"disambiguationData":[OSD([subQ32])]})])],"derivedFrom":makeQuery(id+"F1.opExtrude","CAP_FACE",FACE,{"disambiguationData":[OSD([sQuery(id+"F0.wireOp",EDGE,"E0"),sQuery(id+"F0.wireOp",EDGE,"E1"),subQ28,subQ32,subQ36,sQuery(id+"F0.wireOp",EDGE,"E5"),sQuery(id+"F0.wireOp",EDGE,"E6"),sQuery(id+"F0.wireOp",EDGE,"E7"),subQ33,subQ24,subQ23,subQ22,subQ21,subQ26,subQ30,subQ38,subQ39,subQ40,subQ41,subQ42,subQ43,subQ52,subQ44,subQ45,subQ46,subQ29,subQ53,subQ37,subQ47,subQ34,subQ20,subQ19,subQ18,subQ17,subQ25,subQ16,subQ15,subQ14,subQ13,subQ12,subQ11,subQ10,subQ9,subQ8,subQ7,subQ6,subQ5,subQ4,subQ3,subQ27,subQ31,subQ35,subQ2,subQ1,subQ0,subQ48,sQuery(id+"F0.wireOp",EDGE,"E56"),sQuery(id+"F0.wireOp",EDGE,"E57"),sQuery(id+"F0.wireOp",EDGE,"E58"),sQuery(id+"F0.wireOp",EDGE,"E59"),sQuery(id+"F0.wireOp",EDGE,"E60"),subQ49,subQ50,subQ51])],"isStart":true})});}
            var sketch = newSketch(context, id + "F26", { "sketchPlane" : qUnion([Q0])});
            skLineSegment(sketch, "E83.bottom", {"start": v(-21, -14.97) * mm, "end": v(21, -14.97) * mm});
            skLineSegment(sketch, "E83.top", {"start": v(-21, -16.57) * mm, "end": v(21, -16.57) * mm});
            skLineSegment(sketch, "E83.left", {"start": v(-21, -14.97) * mm, "end": v(-21, -16.57) * mm});
            skLineSegment(sketch, "E83.right", {"start": v(21, -14.97) * mm, "end": v(21, -16.57) * mm});
            skSolve(sketch);
        }
        {
            var Q0;
            Q0 = qSketchRegion(id + "F26", true);
            extrude(context, id + "F27", {"entities" : qUnion([Q0]), "oppositeDirection" : true, "depth" : 64.5 * mm, "offsetDistance" : 25 * mm});
        }
        {
            var Q0;
            Q0=makeQuery(id+"F7.opExtrude","CAP_FACE",FACE,{"disambiguationData":[OSD([sQuery(id+"F6.wireOp",EDGE,"E66.bottom"),sQuery(id+"F6.wireOp",EDGE,"E66.top"),sQuery(id+"F6.wireOp",EDGE,"E66.left"),sQuery(id+"F6.wireOp",EDGE,"E66.right")])],"isStart":false});
            var sketch = newSketch(context, id + "F28", { "sketchPlane" : qUnion([Q0])});
            skLineSegment(sketch, "E84.bottom", {"start": v(-42, 13.82) * mm, "end": v(38.4, 13.82) * mm});
            skLineSegment(sketch, "E84.top", {"start": v(-42, 12.22) * mm, "end": v(38.4, 12.22) * mm});
            skLineSegment(sketch, "E84.left", {"start": v(-42, 13.82) * mm, "end": v(-42, 12.22) * mm});
            skLineSegment(sketch, "E84.right", {"start": v(38.4, 13.82) * mm, "end": v(38.4, 12.22) * mm});
            skSolve(sketch);
        }
        {
            var Q0;
            Q0 = qSketchRegion(id + "F28", true);
            extrude(context, id + "F29", {"entities" : qUnion([Q0]), "oppositeDirection" : true, "depth" : 67 * mm, "offsetDistance" : 25 * mm});
        }
        {
            var Q0;
            Q0=makeQuery(id+"F27.opExtrude","SWEPT_FACE",FACE,{"disambiguationData":[OSD([sQuery(id+"F26.wireOp",EDGE,"E83.top")])]});
            var sketch = newSketch(context, id + "F30", { "sketchPlane" : qUnion([Q0])});
            skLineSegment(sketch, "E85.bottom", {"start": v(-8.5, 63.75) * mm, "end": v(-6.5, 63.75) * mm});
            skLineSegment(sketch, "E85.top", {"start": v(-8.5, 60.75) * mm, "end": v(-6.5, 60.75) * mm});
            skLineSegment(sketch, "E85.left", {"start": v(-8.5, 63.75) * mm, "end": v(-8.5, 60.75) * mm});
            skLineSegment(sketch, "E85.right", {"start": v(-6.5, 63.75) * mm, "end": v(-6.5, 60.75) * mm});
            skLineSegment(sketch, "E86.bottom", {"start": v(6.5, 63.75) * mm, "end": v(8.5, 63.75) * mm});
            skLineSegment(sketch, "E86.top", {"start": v(6.5, 60.75) * mm, "end": v(8.5, 60.75) * mm});
            skLineSegment(sketch, "E86.left", {"start": v(6.5, 63.75) * mm, "end": v(6.5, 60.75) * mm});
            skLineSegment(sketch, "E86.right", {"start": v(8.5, 63.75) * mm, "end": v(8.5, 60.75) * mm});
            skSolve(sketch);
        }
        {
            var Q0;
            Q0 = qSketchRegion(id + "F30", true);
            extrude(context, id + "F31", {"entities" : qUnion([Q0]), "depth" : 0.38 * mm, "offsetDistance" : 25 * mm});
        }
        {
            var Q0;
            Q0=makeQuery(id+"F31.opExtrude","CAP_FACE",FACE,{"disambiguationData":[OSD([sQuery(id+"F30.wireOp",EDGE,"E85.bottom"),sQuery(id+"F30.wireOp",EDGE,"E85.top"),sQuery(id+"F30.wireOp",EDGE,"E85.left"),sQuery(id+"F30.wireOp",EDGE,"E85.right")])],"isStart":false});
            var sketch = newSketch(context, id + "F32", { "sketchPlane" : qUnion([Q0])});
            skCircle(sketch, "E87", {"center": v(-7.5, 62.25) * mm, "radius": 0.5 * mm});
            skCircle(sketch, "E88", {"center": v(7.5, 62.25) * mm, "radius": 0.5 * mm});
            skSolve(sketch);
        }
        {
            var Q0;
            Q0 = qSketchRegion(id + "F32", true);
            extrude(context, id + "F33", {"entities" : qUnion([Q0]), "depth" : 0.2 * mm, "offsetDistance" : 25 * mm});
        }
        {
            var Q0;
            Q0=makeQuery(id+"F33.opExtrude","CAP_EDGE",EDGE,{"disambiguationData":[OSD([sQuery(id+"F32.wireOp",EDGE,"E87")])],"isStart":false});
            var Q1;
            Q1=makeQuery(id+"F33.opExtrude","CAP_EDGE",EDGE,{"disambiguationData":[OSD([sQuery(id+"F32.wireOp",EDGE,"E88")])],"isStart":false});
            fillet(context, id + "F34", {"entities" : qUnion([Q0, Q1]), "radius" : 0.1 * mm, "tangentPropagation" : true, "allowEdgeOverflow" : false});
        }
        {
            var Q0;
            Q0=makeQuery(id+"F27.opExtrude","SWEPT_FACE",FACE,{"disambiguationData":[OSD([sQuery(id+"F26.wireOp",EDGE,"E83.top")])]});
            var sketch = newSketch(context, id + "F35", { "sketchPlane" : qUnion([Q0])});
            skLineSegment(sketch, "E89.bottom", {"start": v(-5.8, 63.85) * mm, "end": v(-4.2, 63.85) * mm});
            skLineSegment(sketch, "E89.top", {"start": v(-5.8, 60.65) * mm, "end": v(-4.2, 60.65) * mm});
            skLineSegment(sketch, "E89.left", {"start": v(-5.8, 63.85) * mm, "end": v(-5.8, 60.65) * mm});
            skLineSegment(sketch, "E89.right", {"start": v(-4.2, 63.85) * mm, "end": v(-4.2, 60.65) * mm});
            skLineSegment(sketch, "E90.bottom", {"start": v(4.2, 63.85) * mm, "end": v(5.8, 63.85) * mm});
            skLineSegment(sketch, "E90.top", {"start": v(4.2, 60.65) * mm, "end": v(5.8, 60.65) * mm});
            skLineSegment(sketch, "E90.left", {"start": v(4.2, 63.85) * mm, "end": v(4.2, 60.65) * mm});
            skLineSegment(sketch, "E90.right", {"start": v(5.8, 63.85) * mm, "end": v(5.8, 60.65) * mm});
            skSolve(sketch);
        }
        {
            var Q0;
            Q0 = qSketchRegion(id + "F35", true);
            extrude(context, id + "F36", {"entities" : qUnion([Q0]), "depth" : 0.25 * mm, "offsetDistance" : 25 * mm});
        }
        {
            var Q0;
            Q0=makeQuery(id+"F27.opExtrude","SWEPT_FACE",FACE,{"disambiguationData":[OSD([sQuery(id+"F26.wireOp",EDGE,"E83.top")])]});
            var sketch = newSketch(context, id + "F37", { "sketchPlane" : qUnion([Q0])});
            skLineSegment(sketch, "E91.bottom", {"start": v(-16.25, 64.5) * mm, "end": v(-14.25, 64.5) * mm});
            skLineSegment(sketch, "E91.left", {"start": v(-16.25, 64.5) * mm, "end": v(-16.25, 62.4) * mm});
            skLineSegment(sketch, "E91.right", {"start": v(-14.25, 64.5) * mm, "end": v(-14.25, 62.4) * mm});
            skLineSegment(sketch, "E92.bottom", {"start": v(14.25, 64.5) * mm, "end": v(16.25, 64.5) * mm});
            skLineSegment(sketch, "E92.left", {"start": v(14.25, 64.5) * mm, "end": v(14.25, 62.4) * mm});
            skLineSegment(sketch, "E92.right", {"start": v(16.25, 64.5) * mm, "end": v(16.25, 62.4) * mm});
            skArc(sketch, "E93", {"start": v(-16.25, 62.4) * mm, "mid": v(-15.25, 61.4) * mm, "end": v(-14.25, 62.4) * mm});
            skArc(sketch, "E94", {"start": v(14.25, 62.4) * mm, "mid": v(15.25, 61.4) * mm, "end": v(16.25, 62.4) * mm});
            skSolve(sketch);
        }
        {
            var Q0;
            Q0 = qSketchRegion(id + "F37", true);
            extrude(context, id + "F38", {"entities" : qUnion([Q0]), "operationType" : NewBodyOperationType.REMOVE, "oppositeDirection" : true, "depth" : 1.65 * mm, "offsetDistance" : 25 * mm});
        }
        {
            var Q0;
            Q0=makeQuery(id+"F27.opExtrude","SWEPT_FACE",FACE,{"disambiguationData":[OSD([sQuery(id+"F26.wireOp",EDGE,"E83.top")])]});
            var sketch = newSketch(context, id + "F39", { "sketchPlane" : qUnion([Q0])});
            skCircle(sketch, "E95", {"center": v(-2.7, 62.25) * mm, "radius": 1 * mm});
            skCircle(sketch, "E96", {"center": v(2.7, 62.25) * mm, "radius": 1 * mm});
            skCircle(sketch, "E97", {"center": v(-10, 62.25) * mm, "radius": 1 * mm});
            skCircle(sketch, "E98", {"center": v(10, 62.25) * mm, "radius": 1 * mm});
            skSolve(sketch);
        }
        {
            var Q0;
            Q0 = qSketchRegion(id + "F39", true);
            extrude(context, id + "F40", {"entities" : qUnion([Q0]), "operationType" : NewBodyOperationType.REMOVE, "oppositeDirection" : true, "depth" : 1.65 * mm, "offsetDistance" : 25 * mm});
        }
        {
            var Q0;
            Q0=makeQuery(id+"F36.opExtrude","CAP_FACE",FACE,{"disambiguationData":[OSD([sQuery(id+"F35.wireOp",EDGE,"E89.bottom"),sQuery(id+"F35.wireOp",EDGE,"E89.top"),sQuery(id+"F35.wireOp",EDGE,"E89.left"),sQuery(id+"F35.wireOp",EDGE,"E89.right")])],"isStart":false});
            var sketch = newSketch(context, id + "F41", { "sketchPlane" : qUnion([Q0])});
            skCircle(sketch, "E99", {"center": v(-5, 62.25) * mm, "radius": 0.8 * mm});
            skSolve(sketch);
        }
        {
            var Q0;
            Q0 = qSketchRegion(id + "F41", true);
            extrude(context, id + "F42", {"entities" : qUnion([Q0]), "operationType" : NewBodyOperationType.ADD, "depth" : 1.55 * mm, "offsetDistance" : 25 * mm});
        }
        {
            var Q0;
            Q0=makeQuery(id+"F42.opExtrude","CAP_EDGE",EDGE,{"disambiguationData":[OSD([sQuery(id+"F41.wireOp",EDGE,"E99")])],"isStart":false});
            fillet(context, id + "F43", {"entities" : qUnion([Q0]), "radius" : 0.8 * mm, "tangentPropagation" : true, "allowEdgeOverflow" : false});
        }
        {
            var Q0;
            Q0=makeQuery(id+"F36.opExtrude","CAP_FACE",FACE,{"disambiguationData":[OSD([sQuery(id+"F35.wireOp",EDGE,"E90.bottom"),sQuery(id+"F35.wireOp",EDGE,"E90.top"),sQuery(id+"F35.wireOp",EDGE,"E90.left"),sQuery(id+"F35.wireOp",EDGE,"E90.right")])],"isStart":false});
            var sketch = newSketch(context, id + "F44", { "sketchPlane" : qUnion([Q0])});
            skCircle(sketch, "E100", {"center": v(5, 62.25) * mm, "radius": 0.8 * mm});
            skSolve(sketch);
        }
        {
            var Q0;
            Q0 = qSketchRegion(id + "F44", true);
            extrude(context, id + "F45", {"entities" : qUnion([Q0]), "operationType" : NewBodyOperationType.ADD, "depth" : 1.55 * mm, "offsetDistance" : 25 * mm});
        }
        {
            var Q0;
            Q0=makeQuery(id+"F45.opExtrude","CAP_EDGE",EDGE,{"disambiguationData":[OSD([sQuery(id+"F44.wireOp",EDGE,"E100")])],"isStart":false});
            fillet(context, id + "F46", {"entities" : qUnion([Q0]), "radius" : 0.8 * mm, "tangentPropagation" : true, "allowEdgeOverflow" : false});
        }
        {
            var Q0;
            Q0=makeQuery(id+"F14.boolean.opBoolean","COPY",EDGE,{"derivedFrom":makeQuery(id+"F14.opExtrude","SWEPT_EDGE",EDGE,{"disambiguationData":[OSD([sQuery(id+"F13.wireOp",EDGE,"E73.top"),sQuery(id+"F13.wireOp",EDGE,"E73.left")])]})});
            var Q1;
            Q1=makeQuery(id+"F14.boolean.opBoolean","COPY",EDGE,{"derivedFrom":makeQuery(id+"F14.opExtrude","SWEPT_EDGE",EDGE,{"disambiguationData":[OSD([sQuery(id+"F13.wireOp",EDGE,"E73.top"),sQuery(id+"F13.wireOp",EDGE,"E73.right")])]})});
            fillet(context, id + "F47", {"entities" : qUnion([Q0, Q1]), "radius" : 1 * mm, "tangentPropagation" : true, "allowEdgeOverflow" : false});
        }
        {
            var Q0;
            Q0 = qSketchRegion(id + "F39", true);
            extrude(context, id + "F48", {"entities" : qUnion([Q0]), "operationType" : NewBodyOperationType.REMOVE, "oppositeDirection" : true, "depth" : 1.65 * mm, "offsetDistance" : 25 * mm});
        }
        {
            var Q0;
            Q0=makeQuery(id+"F33.opExtrude","CAP_FACE",FACE,{"disambiguationData":[OSD([sQuery(id+"F32.wireOp",EDGE,"E87")])],"isStart":false});
            var sketch = newSketch(context, id + "F49", { "sketchPlane" : qUnion([Q0])});
            skLineSegment(sketch, "E101.bottom", {"start": v(-11.5, 64.28) * mm, "end": v(-1.2, 64.28) * mm});
            skLineSegment(sketch, "E101.top", {"start": v(-11.5, 60.28) * mm, "end": v(-1.2, 60.28) * mm});
            skLineSegment(sketch, "E101.left", {"start": v(-11.5, 64.28) * mm, "end": v(-11.5, 60.28) * mm});
            skLineSegment(sketch, "E101.right", {"start": v(-1.2, 64.28) * mm, "end": v(-1.2, 60.28) * mm});
            skSolve(sketch);
        }
        {
            var Q0;
            Q0 = qSketchRegion(id + "F49", true);
            extrude(context, id + "F50", {"entities" : qUnion([Q0]), "depth" : 3 * mm, "offsetDistance" : 25 * mm});
        }
        {
            var Q0;
            Q0=makeQuery(id+"F50.opExtrude","CAP_FACE",FACE,{"disambiguationData":[OSD([sQuery(id+"F49.wireOp",EDGE,"E101.bottom"),sQuery(id+"F49.wireOp",EDGE,"E101.top"),sQuery(id+"F49.wireOp",EDGE,"E101.left"),sQuery(id+"F49.wireOp",EDGE,"E101.right")])],"isStart":false});
            var sketch = newSketch(context, id + "F51", { "sketchPlane" : qUnion([Q0])});
            skCircle(sketch, "E102", {"center": v(-5, 62.25) * mm, "radius": 1.5 * mm});
            skSolve(sketch);
        }
        {
            var Q0;
            Q0 = qSketchRegion(id + "F51", true);
            extrude(context, id + "F52", {"entities" : qUnion([Q0]), "operationType" : NewBodyOperationType.ADD, "depth" : 20 * mm, "offsetDistance" : 25 * mm, "hasDraft" : true, "draftAngle" : 0.2 * degree, "draftPullDirection" : true});
        }
        {
            var Q0;
            Q0=makeQuery(id+"F50.opExtrude","CAP_FACE",FACE,{"disambiguationData":[OSD([sQuery(id+"F49.wireOp",EDGE,"E101.bottom"),sQuery(id+"F49.wireOp",EDGE,"E101.top"),sQuery(id+"F49.wireOp",EDGE,"E101.left"),sQuery(id+"F49.wireOp",EDGE,"E101.right")])],"isStart":true});
            var sketch = newSketch(context, id + "F53", { "sketchPlane" : qUnion([Q0])});
            skCircle(sketch, "E103", {"center": v(2.7, 62.25) * mm, "radius": 0.9 * mm});
            skCircle(sketch, "E104", {"center": v(10, 62.25) * mm, "radius": 0.9 * mm});
            skSolve(sketch);
        }
        {
            var Q0;
            Q0 = qSketchRegion(id + "F53", true);
            extrude(context, id + "F54", {"entities" : qUnion([Q0]), "operationType" : NewBodyOperationType.ADD, "depth" : 3 * mm, "offsetDistance" : 25 * mm, "hasDraft" : true, "draftAngle" : 0.3 * degree, "draftPullDirection" : true});
        }
        {
            var Q0;
            Q0=makeQuery(id+"F54.opExtrude","CAP_EDGE",EDGE,{"disambiguationData":[OSD([sQuery(id+"F53.wireOp",EDGE,"E103")])],"isStart":false});
            var Q1;
            Q1=makeQuery(id+"F54.opExtrude","CAP_EDGE",EDGE,{"disambiguationData":[OSD([sQuery(id+"F53.wireOp",EDGE,"E104")])],"isStart":false});
            fillet(context, id + "F55", {"entities" : qUnion([Q0, Q1]), "radius" : 0.3 * mm, "tangentPropagation" : true, "allowEdgeOverflow" : false});
        }
        {
            var Q0;
            Q0=makeQuery(id+"F50.opExtrude","CAP_FACE",FACE,{"disambiguationData":[OSD([sQuery(id+"F49.wireOp",EDGE,"E101.bottom"),sQuery(id+"F49.wireOp",EDGE,"E101.top"),sQuery(id+"F49.wireOp",EDGE,"E101.left"),sQuery(id+"F49.wireOp",EDGE,"E101.right")])],"isStart":true});
            var sketch = newSketch(context, id + "F56", { "sketchPlane" : qUnion([Q0])});
            skCircle(sketch, "E105", {"center": v(5, 62.25) * mm, "radius": 0.95 * mm});
            skSolve(sketch);
        }
        {
            var Q0;
            Q0 = qSketchRegion(id + "F56", true);
            extrude(context, id + "F57", {"entities" : qUnion([Q0]), "operationType" : NewBodyOperationType.REMOVE, "oppositeDirection" : true, "depth" : 2 * mm, "offsetDistance" : 25 * mm});
        }
        {
            var Q0;
            Q0=makeQuery(id+"F50.opExtrude","CAP_FACE",FACE,{"disambiguationData":[OSD([sQuery(id+"F49.wireOp",EDGE,"E101.bottom"),sQuery(id+"F49.wireOp",EDGE,"E101.top"),sQuery(id+"F49.wireOp",EDGE,"E101.left"),sQuery(id+"F49.wireOp",EDGE,"E101.right")])],"isStart":true});
            var sketch = newSketch(context, id + "F58", { "sketchPlane" : qUnion([Q0])});
            skCircle(sketch, "E106", {"center": v(5, 62.25) * mm, "radius": 0.95 * mm});
            skSolve(sketch);
        }
        {
            var Q0;
            Q0 = qSketchRegion(id + "F58", true);
            extrude(context, id + "F59", {"entities" : qUnion([Q0]), "operationType" : NewBodyOperationType.REMOVE, "oppositeDirection" : true, "depth" : 2.2 * mm, "offsetDistance" : 25 * mm, "hasDraft" : true, "draftAngle" : 0.3 * degree, "draftPullDirection" : true});
        }
        {
            var Q0;
            Q0=makeQuery(id+"F50.opExtrude","SWEPT_EDGE",EDGE,{"disambiguationData":[OSD([sQuery(id+"F49.wireOp",EDGE,"E101.bottom"),sQuery(id+"F49.wireOp",EDGE,"E101.right")])]});
            var Q1;
            Q1=makeQuery(id+"F50.opExtrude","SWEPT_EDGE",EDGE,{"disambiguationData":[OSD([sQuery(id+"F49.wireOp",EDGE,"E101.bottom"),sQuery(id+"F49.wireOp",EDGE,"E101.left")])]});
            var Q2;
            Q2=makeQuery(id+"F50.opExtrude","SWEPT_EDGE",EDGE,{"disambiguationData":[OSD([sQuery(id+"F49.wireOp",EDGE,"E101.top"),sQuery(id+"F49.wireOp",EDGE,"E101.right")])]});
            var Q3;
            Q3=makeQuery(id+"F50.opExtrude","SWEPT_EDGE",EDGE,{"disambiguationData":[OSD([sQuery(id+"F49.wireOp",EDGE,"E101.top"),sQuery(id+"F49.wireOp",EDGE,"E101.left")])]});
            fillet(context, id + "F60", {"entities" : qUnion([Q0, Q1, Q2, Q3]), "radius" : 1 * mm, "tangentPropagation" : true, "allowEdgeOverflow" : false});
        }
        {
            var Q0;
            Q0=makeQuery(id+"F50.opExtrude","CAP_EDGE",EDGE,{"disambiguationData":[OSD([sQuery(id+"F49.wireOp",EDGE,"E101.bottom")])],"isStart":false});
            var Q1;
            Q1=makeQuery(id+"F50.opExtrude","CAP_EDGE",EDGE,{"disambiguationData":[OSD([sQuery(id+"F49.wireOp",EDGE,"E101.bottom")])],"isStart":true});
            fillet(context, id + "F61", {"entities" : qUnion([Q0, Q1]), "radius" : 0.3 * mm, "tangentPropagation" : true, "allowEdgeOverflow" : false});
        }
        {
            var Q0;
            Q0=makeQuery(id+"F52.opExtrude","CAP_EDGE",EDGE,{"disambiguationData":[OSD([sQuery(id+"F51.wireOp",EDGE,"E102")])],"isStart":false});
            fillet(context, id + "F62", {"entities" : qUnion([Q0]), "radius" : 0.3 * mm, "tangentPropagation" : true, "allowEdgeOverflow" : false});
        }
        {
            var Q0;
            Q0=makeQuery(id+"F27.opExtrude","SWEPT_FACE",FACE,{"disambiguationData":[OSD([sQuery(id+"F26.wireOp",EDGE,"E83.top")])]});
            var sketch = newSketch(context, id + "F63", { "sketchPlane" : qUnion([Q0])});
            skCircle(sketch, "E107", {"center": v(-18.08, 56.07) * mm, "radius": 0.6 * mm});
            skCircle(sketch, "E108", {"center": v(-15.54, 56.07) * mm, "radius": 0.6 * mm});
            skCircle(sketch, "E109", {"center": v(-13, 56.07) * mm, "radius": 0.6 * mm});
            skCircle(sketch, "E110", {"center": v(-10.46, 56.07) * mm, "radius": 0.6 * mm});
            skCircle(sketch, "E111", {"center": v(-7.92, 56.07) * mm, "radius": 0.6 * mm});
            skCircle(sketch, "E112", {"center": v(18.08, 56.07) * mm, "radius": 0.6 * mm});
            skCircle(sketch, "E113", {"center": v(15.54, 56.07) * mm, "radius": 0.6 * mm});
            skCircle(sketch, "E114", {"center": v(13, 56.07) * mm, "radius": 0.6 * mm});
            skCircle(sketch, "E115", {"center": v(10.46, 56.07) * mm, "radius": 0.6 * mm});
            skCircle(sketch, "E116", {"center": v(7.92, 56.07) * mm, "radius": 0.6 * mm});
            skSolve(sketch);
        }
        {
            var Q0;
            Q0 = qSketchRegion(id + "F63", true);
            extrude(context, id + "F64", {"entities" : qUnion([Q0]), "operationType" : NewBodyOperationType.REMOVE, "oppositeDirection" : true, "depth" : 1.65 * mm, "offsetDistance" : 25 * mm});
        }
        {
            var Q0;
            Q0=makeQuery(id+"F10.opExtrude","SWEPT_FACE",FACE,{"disambiguationData":[OSD([sQuery(id+"F9.wireOp",EDGE,"E68.bottom")])]});
            var sketch = newSketch(context, id + "F65", { "sketchPlane" : qUnion([Q0])});
            skCircle(sketch, "E117", {"center": v(-18.08, 56.07) * mm, "radius": 0.6 * mm});
            skCircle(sketch, "E118", {"center": v(-15.54, 56.07) * mm, "radius": 0.6 * mm});
            skCircle(sketch, "E119", {"center": v(-13, 56.07) * mm, "radius": 0.6 * mm});
            skCircle(sketch, "E120", {"center": v(-10.46, 56.07) * mm, "radius": 0.6 * mm});
            skCircle(sketch, "E121", {"center": v(-7.92, 56.07) * mm, "radius": 0.6 * mm});
            skCircle(sketch, "E122", {"center": v(7.92, 56.07) * mm, "radius": 0.6 * mm});
            skCircle(sketch, "E123", {"center": v(10.46, 56.07) * mm, "radius": 0.6 * mm});
            skCircle(sketch, "E124", {"center": v(13, 56.07) * mm, "radius": 0.6 * mm});
            skCircle(sketch, "E125", {"center": v(15.54, 56.07) * mm, "radius": 0.6 * mm});
            skCircle(sketch, "E126", {"center": v(18.08, 56.07) * mm, "radius": 0.6 * mm});
            skSolve(sketch);
        }
        {
            var Q0;
            Q0 = qSketchRegion(id + "F65", true);
            extrude(context, id + "F66", {"entities" : qUnion([Q0]), "operationType" : NewBodyOperationType.REMOVE, "oppositeDirection" : true, "depth" : 1.65 * mm, "offsetDistance" : 25 * mm});
        }
        {
            var Q0;
            Q0=makeQuery(id+"F27.opExtrude","SWEPT_FACE",FACE,{"disambiguationData":[OSD([sQuery(id+"F26.wireOp",EDGE,"E83.right")])]});
            var sketch = newSketch(context, id + "F67", { "sketchPlane" : qUnion([Q0])});
            skLineSegment(sketch, "E127.bottom", {"start": v(14.97, 0) * mm, "end": v(16.57, 0) * mm});
            skLineSegment(sketch, "E127.top", {"start": v(14.97, 22.5) * mm, "end": v(16.57, 22.5) * mm});
            skLineSegment(sketch, "E127.left", {"start": v(14.97, 0) * mm, "end": v(14.97, 22.5) * mm});
            skLineSegment(sketch, "E127.right", {"start": v(16.57, 0) * mm, "end": v(16.57, 22.5) * mm});
            skSolve(sketch);
        }
        {
            var Q0;
            Q0 = qSketchRegion(id + "F67", true);
            extrude(context, id + "F68", {"entities" : qUnion([Q0]), "operationType" : NewBodyOperationType.ADD, "depth" : 11.5 * mm, "offsetDistance" : 25 * mm});
        }
    });
